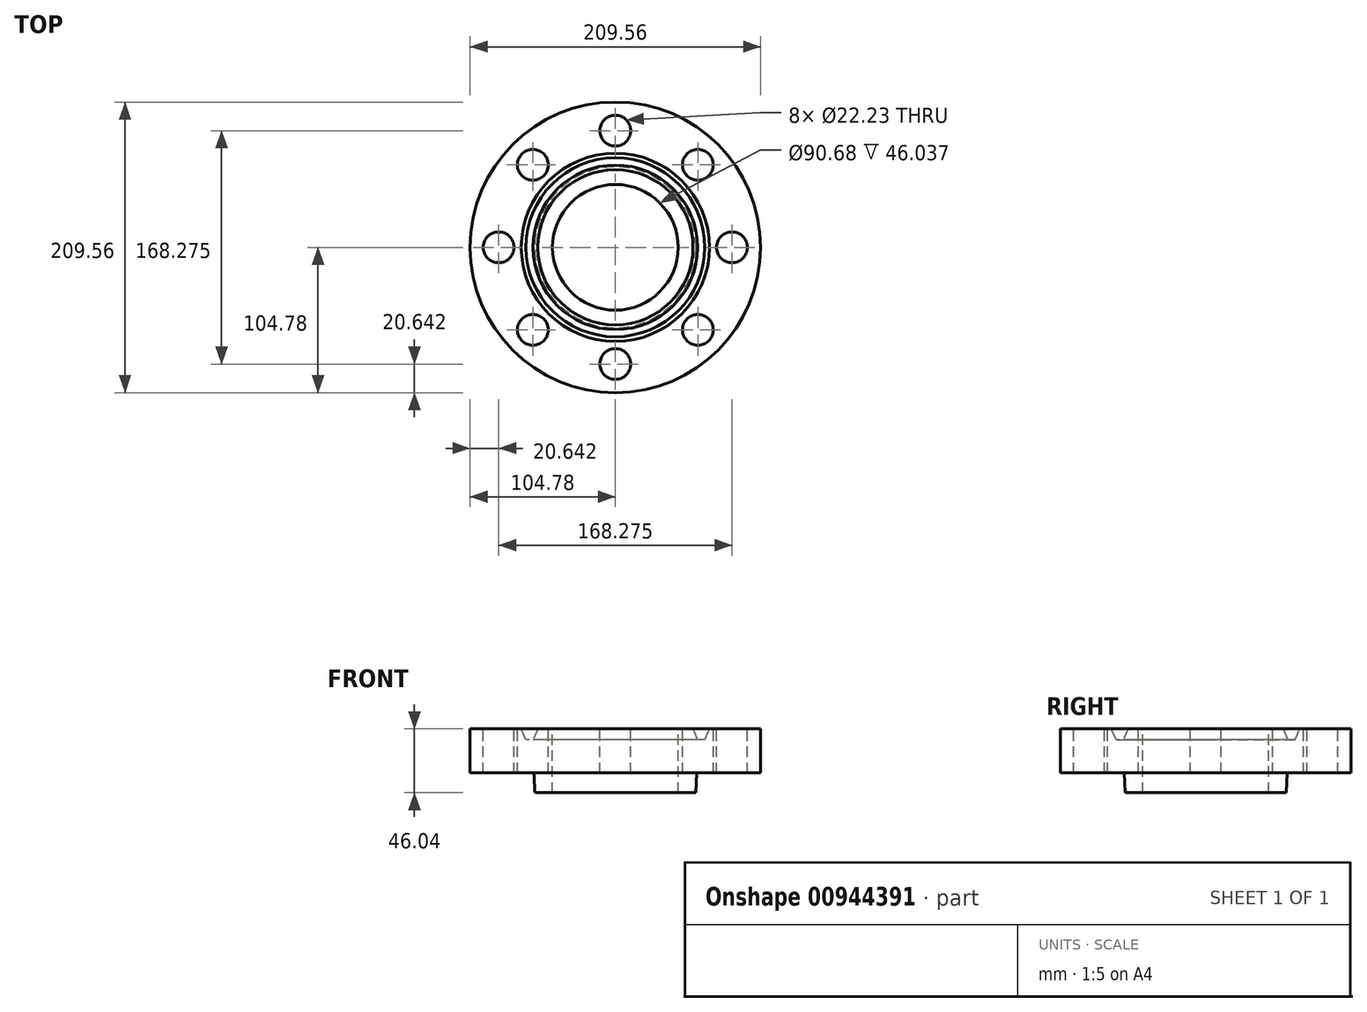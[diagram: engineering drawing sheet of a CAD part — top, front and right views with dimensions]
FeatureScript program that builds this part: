
annotation { "Feature Type Name" : "Feature", "Feature Type Description" : "" }
export const myFeature = defineFeature(function(context is Context, id is Id, definition is map)
    precondition{}
    {
        {
            var Q0;
            Q0=qCreatedBy(makeId("Top.planeOp"),FACE);
            var sketch = newSketch(context, id + "F0", { "sketchPlane" : qUnion([Q0])});
            skCircle(sketch, "E0", {"center": v(0, 0) * mm, "radius": 104.78 * mm});
            skSolve(sketch);
        }
        {
            var Q0;
            Q0 = qSketchRegion(id + "F0", true);
            extrude(context, id + "F1", {"entities" : qUnion([Q0]), "oppositeDirection" : true, "depth" : 31.75 * mm, "offsetDistance" : 25 * mm});
        }
        {
            var Q0;
            Q0=makeQuery(id+"F1.opExtrude","CAP_FACE",FACE,{"disambiguationData":[OSD([sQuery(id+"F0.wireOp",EDGE,"E0")])],"isStart":false});
            var sketch = newSketch(context, id + "F2", { "sketchPlane" : qUnion([Q0])});
            skCircle(sketch, "E1", {"center": v(0, 0) * mm, "radius": 58.74 * mm});
            skSolve(sketch);
        }
        {
            var Q0;
            Q0 = qSketchRegion(id + "F2", true);
            extrude(context, id + "F3", {"entities" : qUnion([Q0]), "operationType" : NewBodyOperationType.ADD, "depth" : 14.29 * mm, "offsetDistance" : 25 * mm, "hasDraft" : true, "draftAngle" : 3 * degree, "draftPullDirection" : true});
        }
        {
            var Q0;
            Q0=makeQuery(id+"F1.opExtrude","CAP_FACE",FACE,{"disambiguationData":[OSD([sQuery(id+"F0.wireOp",EDGE,"E0")])],"isStart":true});
            var sketch = newSketch(context, id + "F4", { "sketchPlane" : qUnion([Q0])});
            skCircle(sketch, "E2", {"center": v(0, 0) * mm, "radius": 45.34 * mm});
            skSolve(sketch);
        }
        {
            var Q0;
            Q0 = qSketchRegion(id + "F4", true);
            extrude(context, id + "F5", {"entities" : qUnion([Q0]), "operationType" : NewBodyOperationType.REMOVE, "endBound" : BoundingType.THROUGH_ALL, "oppositeDirection" : true, "depth" : 25 * mm, "offsetDistance" : 25 * mm});
        }
        {
            var Q0;
            Q0=qCreatedBy(makeId("Front.planeOp"),FACE);
            var sketch = newSketch(context, id + "F6", { "sketchPlane" : qUnion([Q0])});
            skPoint(sketch, "E3", {"position": v(61.91, 0) * mm});
            skLineSegment(sketch, "E4", {"start": v(61.91, 0) * mm, "end": v(67.87, 0) * mm});
            skLineSegment(sketch, "E5", {"start": v(55.96, 0) * mm, "end": v(61.91, 0) * mm});
            skLineSegment(sketch, "E6", {"start": v(61.91, 0) * mm, "end": v(61.91, -7.94) * mm});
            skLineSegment(sketch, "E7", {"start": v(55.96, 0) * mm, "end": v(59.33, -7.94) * mm});
            skLineSegment(sketch, "E8.MirrorCS", {"start": v(67.87, 0) * mm, "end": v(64.5, -7.94) * mm});
            skLineSegment(sketch, "E9", {"start": v(59.33, -7.94) * mm, "end": v(64.5, -7.94) * mm});
            skSolve(sketch);
        }
        {
            var Q0;
            Q0=makeQuery(id+"F1.opExtrude","CAP_FACE",FACE,{"disambiguationData":[OSD([sQuery(id+"F0.wireOp",EDGE,"E0")])],"isStart":true});
            var sketch = newSketch(context, id + "F7", { "sketchPlane" : qUnion([Q0])});
            skCircle(sketch, "E10", {"center": v(0, 0) * mm, "radius": 61.91 * mm});
            skSolve(sketch);
        }
        {
            var Q0;
            Q0 = qSketchRegion(id + "F6", true);
            var Q1;
            Q1=sQuery(id+"F7.wireOp",EDGE,"E10");
            revolve(context, id + "F8", {"operationType" : NewBodyOperationType.REMOVE, "surfaceOperationType" : NewSurfaceOperationType.NEW, "entities" : qUnion([Q0]), "axis" : qUnion([Q1]), "revolveType" : RevolveType.FULL, "oppositeDirection" : true});
        }
        {
            var Q0;
            {var subQ0=sQuery(id+"F0.wireOp",EDGE,"E0");Q0=makeQuery(id+"F8.boolean.opBoolean","SPLIT",FACE,{"disambiguationData":[TD([makeQuery(id+"F1.opExtrude","SWEPT_FACE",FACE,{"disambiguationData":[OSD([subQ0])]})])],"derivedFrom":makeQuery(id+"F1.opExtrude","CAP_FACE",FACE,{"disambiguationData":[OSD([subQ0])],"isStart":true})});}
            var sketch = newSketch(context, id + "F9", { "sketchPlane" : qUnion([Q0])});
            skCircle(sketch, "E11", {"center": v(0, 0) * mm, "radius": 84.14 * mm});
            skCircle(sketch, "E12", {"center": v(84.14, 0) * mm, "radius": 11.11 * mm});
            skCircle(sketch, "E13.1.0", {"center": v(59.5, 59.5) * mm, "radius": 11.11 * mm});
            skCircle(sketch, "E13.2.0", {"center": v(0, 84.14) * mm, "radius": 11.11 * mm});
            skCircle(sketch, "E13.3.0", {"center": v(-59.5, 59.5) * mm, "radius": 11.11 * mm});
            skCircle(sketch, "E13.4.0", {"center": v(-84.14, 0) * mm, "radius": 11.11 * mm});
            skCircle(sketch, "E13.5.0", {"center": v(-59.5, -59.5) * mm, "radius": 11.11 * mm});
            skCircle(sketch, "E13.6.0", {"center": v(0, -84.14) * mm, "radius": 11.11 * mm});
            skCircle(sketch, "E13.7.0", {"center": v(59.5, -59.5) * mm, "radius": 11.11 * mm});
            skSolve(sketch);
        }
        {
            var Q0;
            Q0=sQuery(id+"F9.wireOp",VERTEX,"E13.1.0.center");
            var Q1;
            Q1=sQuery(id+"F9.wireOp",VERTEX,"E12.center");
            var Q2;
            Q2=sQuery(id+"F9.wireOp",VERTEX,"E13.7.0.center");
            var Q3;
            Q3=sQuery(id+"F9.wireOp",VERTEX,"E13.6.0.center");
            var Q4;
            Q4=sQuery(id+"F9.wireOp",VERTEX,"E13.5.0.center");
            var Q5;
            Q5=sQuery(id+"F9.wireOp",VERTEX,"E13.4.0.center");
            var Q6;
            Q6=sQuery(id+"F9.wireOp",VERTEX,"E13.3.0.center");
            var Q7;
            Q7=sQuery(id+"F9.wireOp",VERTEX,"E13.2.0.center");
            var Q8;
            Q8=makeQuery(id+"F1.opExtrude","SWEPT_BODY",BODY,{"disambiguationData":[OSD([sQuery(id+"F0.wireOp",EDGE,"E0")])]});
            hole(context, id + "F10", {"style" : HoleStyle.SIMPLE, "endStyle" : HoleEndStyle.THROUGH, "holeDiameter" : 22.23 * mm, "majorDiameter" : 5 * mm, "isTappedThrough" : true, "tappedDepth" : 12 * mm, "tapClearance" : 3, "locations" : qUnion([Q0, Q1, Q2, Q3, Q4, Q5, Q6, Q7]), "scope" : qUnion([Q8])});
        }
    });
